annotation { "Feature Type Name" : "Feature", "Feature Type Description" : "" }
export const myFeature = defineFeature(function(context is Context, id is Id, definition is map)
    precondition{}
    {
        {
            var Q0;
            Q0=qCreatedBy(makeId("Top.planeOp"),FACE);
            var sketch = newSketch(context, id + "F0", { "sketchPlane" : qUnion([Q0])});
            skLineSegment(sketch, "E0.bottom", {"start": v(36.45, -26.99) * mm, "end": v(-36.45, -26.99) * mm});
            skLineSegment(sketch, "E0.top", {"start": v(36.45, 26.99) * mm, "end": v(-36.45, 26.99) * mm});
            skLineSegment(sketch, "E0.left", {"start": v(42.8, -20.64) * mm, "end": v(42.8, 20.64) * mm});
            skLineSegment(sketch, "E0.right", {"start": v(-42.8, -20.64) * mm, "end": v(-42.8, 20.64) * mm});
            skPoint(sketch, "E0.middle", {"position": v(0, 0) * mm});
            skPoint(sketch, "E1.visualSharp", {"position": v(-42.8, 26.99) * mm});
            skArc(sketch, "E1.filletArc", {"start": v(-36.45, 26.99) * mm, "mid": v(-40.94, 25.13) * mm, "end": v(-42.8, 20.64) * mm});
            skPoint(sketch, "E2.visualSharp", {"position": v(42.8, 26.99) * mm});
            skArc(sketch, "E2.filletArc", {"start": v(42.8, 20.64) * mm, "mid": v(40.94, 25.13) * mm, "end": v(36.45, 26.99) * mm});
            skPoint(sketch, "E3.visualSharp", {"position": v(42.8, -26.99) * mm});
            skArc(sketch, "E3.filletArc", {"start": v(36.45, -26.99) * mm, "mid": v(40.94, -25.13) * mm, "end": v(42.8, -20.64) * mm});
            skPoint(sketch, "E4.visualSharp", {"position": v(-42.8, -26.99) * mm});
            skArc(sketch, "E4.filletArc", {"start": v(-42.8, -20.64) * mm, "mid": v(-40.94, -25.13) * mm, "end": v(-36.45, -26.99) * mm});
            skSolve(sketch);
        }
        {
            var Q0;
            Q0 = qSketchRegion(id + "F0", true);
            extrude(context, id + "F1", {"entities" : qUnion([Q0]), "depth" : 1 * mm, "offsetDistance" : 25.4 * mm});
        }
        {
            var Q0;
            Q0=qCreatedBy(makeId("Top.planeOp"),FACE);
            var sketch = newSketch(context, id + "F2", { "sketchPlane" : qUnion([Q0])});
            skText(sketch, "E5", { "text": "Colin Strecker\n603-801-0477", "fontName": "Arimo-Regular.ttf"});
            const initialGuessF2  = {"E5": [-0.0381, 0.0142, 1, 0, 0.00866]};
            skSetInitialGuess(sketch, initialGuessF2);
            skSolve(sketch);
        }
        {
            var Q0;
            Q0 = qSketchRegion(id + "F2", true);
            extrude(context, id + "F3", {"entities" : qUnion([Q0]), "operationType" : NewBodyOperationType.ADD, "depth" : 2 * mm, "offsetDistance" : 25.4 * mm});
        }
    });